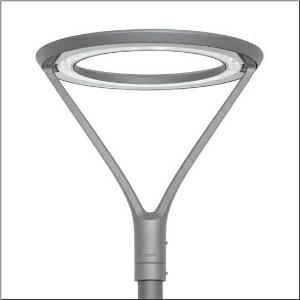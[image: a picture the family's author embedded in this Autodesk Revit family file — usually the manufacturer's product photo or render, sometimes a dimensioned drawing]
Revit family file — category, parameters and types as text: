
# Revit family: dl_r__20___pl1_2s_5xa512836s008p_4065
name_source: partatom
category: Lighting Fixtures
units: mm (PartAtom-declared; Revit-internal decimal feet)

## family parameters
Cut with Voids When Loaded = No
Host = Face
Light Source = No
Part Type = Normal
Room Calculation Point = No
Round Connector Dimension = Use Diameter
Shared = No

## types (1)
- --- (1 x LED, 4250 lm, 40.6 W, 2700K)
    Apparent Load = 41 VA
    CIE Flux Codes = 33 78 99 100 100
    Color Rendering = 70
    Color Temperature = 2700K
    Default Elevation = 1800 mm
    Description = DL® 20, mast luminaire, primary light control with reflector, highly specular, primary optical cover: cover, of toughened safety glass of clear glass with excellent transmission level, light distribution: PL1.2s, light emission: direct distribution, primary light characteristic: symmetric, installation type: post-top, LED, High Power LED, rated luminous flux: 4.250lm, luminous efficacy: 105lm/W, light colour: 727, colour temperature: 2700K, control gear: Plus, control: flexible luminous flux parameterisation, time-dependent luminous flux control, constant luminous flux control, digital communication interface, power reduction, overheat protection, electronic power reduction, mains connection: 220..240V, 50/60Hz, connection cable pre-assembled, cable length: 5m, start of lifetime: 41W, end of service life: 42W, reduction: 20W, luminaire housing, upper part, of cast aluminium, powder-coated, Siteco® metallic grey (DB 702S), diameter: 690mm, height: 690mm, spigot size: 76mm (post-top), mounting height: 4..6m, luminaire housing, of cast aluminium, powder-coated, Siteco® metallic grey (DB 702S), equipment: Power, protection rating (complete): IP66, insulation class (complete): insulation class II (safety insulation), certification: CE, ENEC, VDE, impact resistance: IK08, permissible operating ambient temperature: -25..+30°C, standard-compliant lighting for roads and squares, packaging unit: 1 piece

Light Distribution: PL1.2s
    Height = 690 mm
    Lamp = 1 x LED
    Lamp Light Flux = 4250 lm
    Lamp Power = 40.6 W
    Lamp count = 1
    Length = 690 mm
    Luminous efficacy = 105 lm/W
    Manufacturer = Siteco
    ModVariant = No
    Model = 5XA512836S008P
    Number of Poles = 1
    OnlyDefault = Yes
    Power Factor = 1
    Product Name = DL® 20 | PL1.2s
    Product group = mast luminaire | pylon top
    ProductGroupID = 6100
    Protection Class = Protection class II
    Protection Degree = IP 66
    RLX_Detail_Level = 1
    RLX_Emergency_Light_Flux = 0 lm
    RLX_Emergency_Type = 0
    RLX_Emergency_Type_DB = No
    RlxData = <blob elided: 204289 chars, md5=008a50ac>
    Socket = socket
    Standby Power = 0 W
    System Light Flux = 4250 lm
    System Power = 41 W
    Type Comments = factory setting: luminous flux: 100 % | dim-lin: 254 | 549 mA
    Type Image = l_1006001.jpg
    URL = http://relux.com
    VarID = @adj_098307
    Voltage = 0 V
    Weight = 0.00 kg
    Width = 0 mm  [stored 0 ft]

note: [stored X ft] marks values corroborated as IEEE doubles in the binary element streams (Revit-internal decimal feet)

## geometry (parser evidence)
native form markers: Blend x4, Sweep x11
no freeform markers — native parametric forms only
